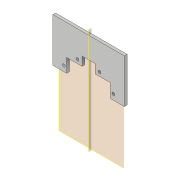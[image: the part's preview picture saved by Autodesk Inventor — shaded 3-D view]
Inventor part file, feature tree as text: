
AUTODESK INVENTOR PART (.ipt)
format: ipt  version: 2018 (Build 220112000, 112)  size: 227,840 bytes
history: native  units: in
note: dims shown in document units (in); Inventor stores cm internally (conversion verified against a paired STEP export)
features: reference x9, sketch x4, other x3, plane x2, extrude x2, hole x1
ambient origin geometry x8: Origin, YZ Plane, XZ Plane, XY Plane, X Axis, Y Axis, Z Axis, Center Point
bodies: Solid1 (feature_tree)
feature tree (21):
  plane  "Work Plane1"
  sketch  "Sketch1"  dims[d0=0.5in d1=0.5in]
  extrude  "Extrusion1"  Depth=0.5in
  hole  "Hole1"  [1 undecoded]
  extrude  "Extrusion3"  Depth=0.75in
  plane  "Work Plane2"
  reference  "Reference1"
  reference  "Reference2"
  reference  "Reference3"
  reference  "Reference4"
  reference  "Reference5"
  reference  "Reference6"
  reference  "Reference7"
  sketch  "Sketch2"  dims[d2=0.5in d3=3.5in]
  sketch  "Sketch3"  dims[d4=0.75in d5=0.75in]
  reference  "Reference8"
  reference  "Reference9"
  sketch  "Sketch5"  dims[d6=1.25in d7=0.6in d8=0.6in d9=0.25in d10=0.0in d11=0.25in d12=0.75in d13=0.375in d14=0.25in d15=0.5635in d16=1.0in d17=0.8108in d26=0.5in d27=0.5in d28=0.5in d29=0.25in d30=0.0in]
  parser-record x1  (decoder bookkeeping rows leaked as tree rows — omitted from the tree; the rows remain in map.json)
  other  "Robot.iam"
  other  "WCP_DS_-_3_CIM_WCD_Base_Kit_w_PTO:2"
note: 1 required parameter value undecoded (feature->parameter linkage not recoverable at this tier; creation-order binding heuristic only, values carry confidence <= 0.55)
note: 1 file-system path scrubbed to <path> (originals preserved in map.json)
